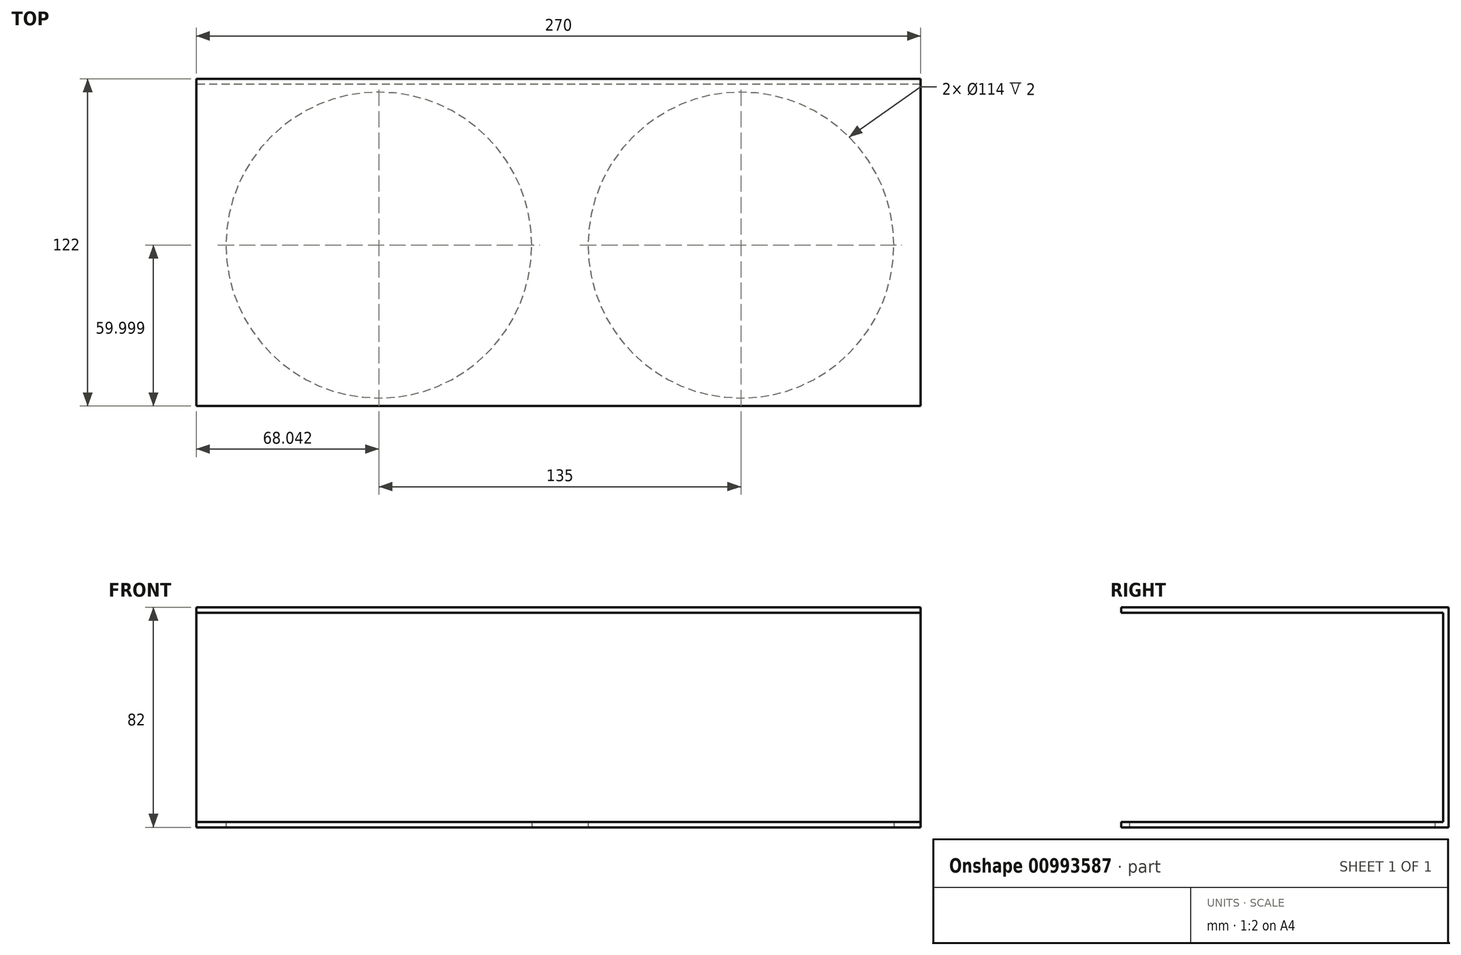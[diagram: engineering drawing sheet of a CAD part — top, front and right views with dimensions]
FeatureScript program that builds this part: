
annotation { "Feature Type Name" : "Feature", "Feature Type Description" : "" }
export const myFeature = defineFeature(function(context is Context, id is Id, definition is map)
    precondition{}
    {
        {
            var Q0;
            Q0=qCreatedBy(makeId("Top.planeOp"),FACE);
            var sketch = newSketch(context, id + "F0", { "sketchPlane" : qUnion([Q0])});
            skLineSegment(sketch, "E0.bottom", {"start": v(-121.33, 61.5) * mm, "end": v(148.67, 61.5) * mm});
            skLineSegment(sketch, "E0.top", {"start": v(-121.33, -58.5) * mm, "end": v(148.67, -58.5) * mm});
            skLineSegment(sketch, "E0.left", {"start": v(-121.33, 61.5) * mm, "end": v(-121.33, -58.5) * mm});
            skLineSegment(sketch, "E0.right", {"start": v(148.67, 61.5) * mm, "end": v(148.67, -58.5) * mm});
            skCircle(sketch, "E1", {"center": v(-53.29, 1.5) * mm, "radius": 57 * mm});
            skCircle(sketch, "E2", {"center": v(81.71, 1.5) * mm, "radius": 57 * mm});
            skLineSegment(sketch, "E3", {"start": v(-121.33, 61.5) * mm, "end": v(-121.33, 63.5) * mm});
            skLineSegment(sketch, "E4", {"start": v(-121.33, 63.5) * mm, "end": v(148.67, 63.5) * mm});
            skLineSegment(sketch, "E5", {"start": v(148.67, 63.5) * mm, "end": v(148.67, 61.5) * mm});
            skSolve(sketch);
        }
        {
            var Q0;
            Q0 = qSketchRegion(id + "F0", true);
            extrude(context, id + "F1", {"entities" : qUnion([Q0]), "depth" : 2 * mm, "offsetDistance" : 25 * mm});
        }
        {
            var Q0;
            Q0=makeQuery(id+"F0.imprint","IMPRINT",FACE,{"disambiguationData":[TD([[makeQuery(id+"F0.imprint","IMPRINT",EDGE,{"derivedFrom":sQuery(id+"F0.wireOp",EDGE,"E0.bottom")}),1.0]])]});
            extrude(context, id + "F2", {"entities" : qUnion([Q0]), "operationType" : NewBodyOperationType.ADD, "depth" : 80 * mm, "offsetDistance" : 25 * mm});
        }
        {
            var Q0;
            Q0=makeQuery(id+"F2.opExtrude","SWEPT_FACE",FACE,{"disambiguationData":[OSD([sQuery(id+"F0.wireOp",EDGE,"E0.bottom")])]});
            var sketch = newSketch(context, id + "F3", { "sketchPlane" : qUnion([Q0])});
            skLineSegment(sketch, "E6", {"start": v(148.67, 80) * mm, "end": v(148.67, 82) * mm});
            skLineSegment(sketch, "E7", {"start": v(148.67, 82) * mm, "end": v(-121.33, 82) * mm});
            skLineSegment(sketch, "E8", {"start": v(-121.33, 82) * mm, "end": v(-121.33, 80) * mm});
            skSolve(sketch);
        }
        {
            var Q0;
            Q0=makeQuery(id+"F3.imprint","IMPRINT",FACE,{"disambiguationData":[TD([[makeQuery(id+"F3.imprint","IMPRINT",EDGE,{"derivedFrom":sQuery(id+"F3.wireOp",EDGE,"E6")}),1.0]])]});
            extrude(context, id + "F4", {"entities" : qUnion([Q0]), "operationType" : NewBodyOperationType.ADD, "depth" : 120 * mm, "offsetDistance" : 25 * mm, "hasSecondDirection" : true, "secondDirectionOppositeDirection" : true, "secondDirectionDepth" : 2 * mm});
        }
    });
